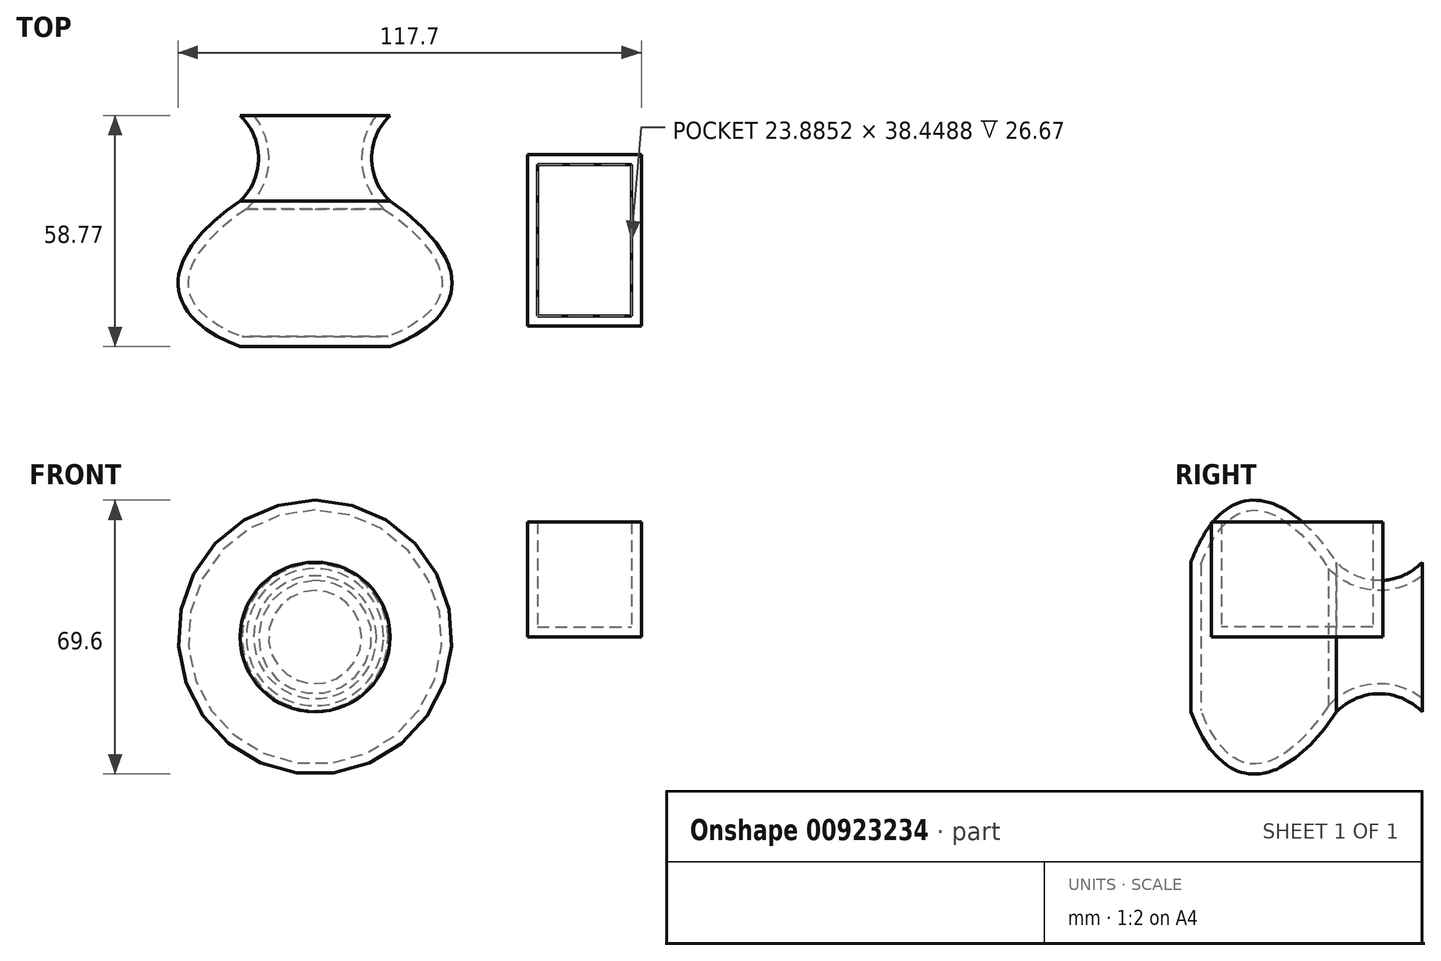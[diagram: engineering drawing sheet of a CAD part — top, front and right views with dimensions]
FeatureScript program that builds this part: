
annotation { "Feature Type Name" : "Feature", "Feature Type Description" : "" }
export const myFeature = defineFeature(function(context is Context, id is Id, definition is map)
    precondition{}
    {
        {
            var Q0;
            Q0=qCreatedBy(makeId("Top.planeOp"),FACE);
            var sketch = newSketch(context, id + "F0", { "sketchPlane" : qUnion([Q0])});
            skLineSegment(sketch, "E0", {"start": v(-57.92, 30.23) * mm, "end": v(-38.9, 30.23) * mm});
            skLineSegment(sketch, "E1", {"start": v(-38.9, 30.23) * mm, "end": v(-38.9, -28.54) * mm});
            skLineSegment(sketch, "E2", {"start": v(-38.9, -28.54) * mm, "end": v(-57.92, -28.54) * mm});
            skFitSpline(sketch, "E3", {"points": [v(-57.92, -28.54) * mm, v(-57.92, 8.46) * mm], "startDerivative": vector(-64.05, 24.1) * mm, "endDerivative": vector(62.15, 41.85) * mm});
            skArc(sketch, "E4", {"start": v(-57.92, 8.46) * mm, "mid": v(-53.27, 19.34) * mm, "end": v(-57.92, 30.23) * mm});
            skSolve(sketch);
        }
        {
            var Q0;
            Q0=qCreatedBy(makeId("Top.planeOp"),FACE);
            var sketch = newSketch(context, id + "F1", { "sketchPlane" : qUnion([Q0])});
            skLineSegment(sketch, "E5.bottom", {"start": v(11.96, 22.98) * mm, "end": v(47.4, 22.98) * mm});
            skLineSegment(sketch, "E5.top", {"start": v(11.96, -26.53) * mm, "end": v(47.4, -26.53) * mm});
            skLineSegment(sketch, "E5.left", {"start": v(11.96, 22.98) * mm, "end": v(11.96, -26.53) * mm});
            skLineSegment(sketch, "E5.right", {"start": v(47.4, 22.98) * mm, "end": v(47.4, -26.53) * mm});
            skLineSegment(sketch, "E6.bottom", {"start": v(15.04, 20.23) * mm, "end": v(44, 20.23) * mm});
            skLineSegment(sketch, "E6.top", {"start": v(15.04, -23.3) * mm, "end": v(44, -23.3) * mm});
            skLineSegment(sketch, "E6.left", {"start": v(15.04, 20.23) * mm, "end": v(15.04, -23.3) * mm});
            skLineSegment(sketch, "E6.right", {"start": v(44, 20.23) * mm, "end": v(44, -23.3) * mm});
            skSolve(sketch);
        }
        {
            var Q0;
            Q0=makeQuery(id+"F1.imprint","IMPRINT",FACE,{"disambiguationData":[TD([[makeQuery(id+"F1.imprint","IMPRINT",EDGE,{"derivedFrom":sQuery(id+"F1.wireOp",EDGE,"E6.bottom")}),-1.0]])]});
            extrude(context, id + "F2", {"entities" : qUnion([Q0]), "depth" : 3.8 * mm, "offsetDistance" : 25.4 * mm});
        }
        {
            var Q0;
            Q0=makeQuery(id+"F2.opExtrude","CAP_FACE",FACE,{"disambiguationData":[OSD([sQuery(id+"F1.wireOp",EDGE,"E6.bottom"),sQuery(id+"F1.wireOp",EDGE,"E6.top"),sQuery(id+"F1.wireOp",EDGE,"E6.left"),sQuery(id+"F1.wireOp",EDGE,"E6.right")])],"isStart":false});
            extrude(context, id + "F3", {"entities" : qUnion([Q0]), "operationType" : NewBodyOperationType.ADD, "depth" : 25.4 * mm, "offsetDistance" : 25.4 * mm});
        }
        {
            var Q0;
            Q0=makeQuery(id+"F3.opExtrude","CAP_FACE",FACE,{"disambiguationData":[OSD([sQuery(id+"F1.wireOp",EDGE,"E6.bottom"),sQuery(id+"F1.wireOp",EDGE,"E6.top"),sQuery(id+"F1.wireOp",EDGE,"E6.left"),sQuery(id+"F1.wireOp",EDGE,"E6.right")])],"isStart":false});
            shell(context, id + "F4", {"entities" : qUnion([Q0]), "thickness" : 2.54 * mm});
        }
        {
            var Q0;
            Q0=makeQuery(id+"F0.imprint","IMPRINT",FACE,{"disambiguationData":[TD([[makeQuery(id+"F0.imprint","IMPRINT",EDGE,{"derivedFrom":sQuery(id+"F0.wireOp",EDGE,"E0")}),-1.0]])]});
            var Q1;
            Q1=sQuery(id+"F0.wireOp",EDGE,"E1");
            revolve(context, id + "F5", {"surfaceOperationType" : NewSurfaceOperationType.NEW, "entities" : qUnion([Q0]), "axis" : qUnion([Q1]), "revolveType" : RevolveType.FULL});
        }
        {
            var Q0;
            Q0=makeQuery(id+"F5.opRevolve","SWEPT_FACE",FACE,{"disambiguationData":[OSD([sQuery(id+"F0.wireOp",EDGE,"E0")])]});
            shell(context, id + "F6", {"entities" : qUnion([Q0]), "thickness" : 2.54 * mm});
        }
    });
